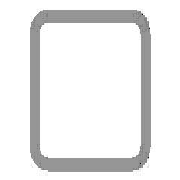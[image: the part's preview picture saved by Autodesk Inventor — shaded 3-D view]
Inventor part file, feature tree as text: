
AUTODESK INVENTOR PART (.ipt)
format: ipt  version: 2024 (Build 280153000, 153)  size: 129,024 bytes
history: native  units: mm (DEFAULTED — no unit token found)
features: other x4, extrude x1, sketch x1, plane x1
ambient origin geometry x8: Origin, YZ Plane, XZ Plane, XY Plane, X Axis, Y Axis, Z Axis, Center Point
bodies: Solid1 (feature_tree)
feature tree (7):
  parser-record x1  (decoder bookkeeping rows leaked as tree rows — omitted from the tree; the rows remain in map.json)
  other  "Driven Length"
  other  "Plano inicial"
  other  "Plano final"
  extrude  "Cuerpo"  TaperAngle=0.0deg  [1 undecoded]
  sketch  "Sketch3"  dims[d3=1150.0mm d4=0.0mm d10=50.8mm d11=50.8mm d12=3.175mm d13=-0.0mm d14=1150.0mm d15=25.4mm d16=25.4mm d17=6.35mm d18=90.0deg d19=1150.0mm]
  plane  "Work Plane3"
note: 1 required parameter value undecoded (feature->parameter linkage not recoverable at this tier; creation-order binding heuristic only, values carry confidence <= 0.55)
